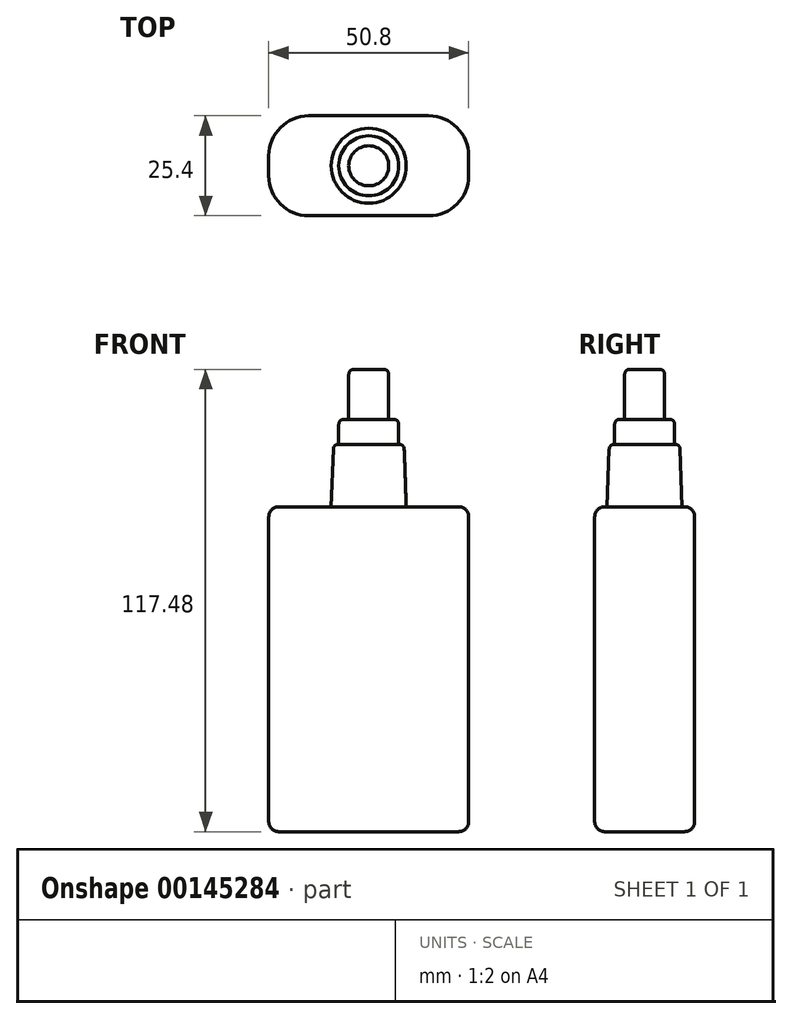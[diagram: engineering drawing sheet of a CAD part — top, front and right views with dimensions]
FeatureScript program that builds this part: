
annotation { "Feature Type Name" : "Feature", "Feature Type Description" : "" }
export const myFeature = defineFeature(function(context is Context, id is Id, definition is map)
    precondition{}
    {
        {
            var Q0;
            Q0=qCreatedBy(makeId("Top.planeOp"),FACE);
            var sketch = newSketch(context, id + "F0", { "sketchPlane" : qUnion([Q0])});
            skLineSegment(sketch, "E0.bottom", {"start": v(-15.24, 12.7) * mm, "end": v(15.24, 12.7) * mm});
            skLineSegment(sketch, "E0.top", {"start": v(-15.24, -12.7) * mm, "end": v(15.24, -12.7) * mm});
            skLineSegment(sketch, "E0.left", {"start": v(-25.4, 2.54) * mm, "end": v(-25.4, -2.54) * mm});
            skLineSegment(sketch, "E0.right", {"start": v(25.4, 2.54) * mm, "end": v(25.4, -2.54) * mm});
            skPoint(sketch, "E0.middle", {"position": v(0, 0) * mm});
            skPoint(sketch, "E1.visualSharp", {"position": v(-25.4, 12.7) * mm});
            skArc(sketch, "E1.filletArc", {"start": v(-15.24, 12.7) * mm, "mid": v(-22.42, 9.72) * mm, "end": v(-25.4, 2.54) * mm});
            skPoint(sketch, "E2.visualSharp", {"position": v(-25.4, -12.7) * mm});
            skArc(sketch, "E2.filletArc", {"start": v(-25.4, -2.54) * mm, "mid": v(-22.42, -9.72) * mm, "end": v(-15.24, -12.7) * mm});
            skPoint(sketch, "E3.visualSharp", {"position": v(25.4, 12.7) * mm});
            skArc(sketch, "E3.filletArc", {"start": v(25.4, 2.54) * mm, "mid": v(22.42, 9.72) * mm, "end": v(15.24, 12.7) * mm});
            skPoint(sketch, "E4.visualSharp", {"position": v(25.4, -12.7) * mm});
            skArc(sketch, "E4.filletArc", {"start": v(15.24, -12.7) * mm, "mid": v(22.42, -9.72) * mm, "end": v(25.4, -2.54) * mm});
            skSolve(sketch);
        }
        {
            var Q0;
            Q0=makeQuery(id+"F0.imprint","IMPRINT",FACE,{"disambiguationData":[TD([[makeQuery(id+"F0.imprint","IMPRINT",EDGE,{"derivedFrom":sQuery(id+"F0.wireOp",EDGE,"E0.bottom")}),-1.0]])]});
            extrude(context, id + "F1", {"entities" : qUnion([Q0]), "depth" : 82.55 * mm});
        }
        {
            var Q0;
            Q0=makeQuery(id+"F1.opExtrude","CAP_FACE",FACE,{"disambiguationData":[OSD([sQuery(id+"F0.wireOp",EDGE,"E0.bottom"),sQuery(id+"F0.wireOp",EDGE,"E0.top"),sQuery(id+"F0.wireOp",EDGE,"E0.left"),sQuery(id+"F0.wireOp",EDGE,"E0.right"),sQuery(id+"F0.wireOp",EDGE,"E1.filletArc"),sQuery(id+"F0.wireOp",EDGE,"E2.filletArc"),sQuery(id+"F0.wireOp",EDGE,"E3.filletArc"),sQuery(id+"F0.wireOp",EDGE,"E4.filletArc")])],"isStart":false});
            var sketch = newSketch(context, id + "F2", { "sketchPlane" : qUnion([Q0])});
            skCircle(sketch, "E5", {"center": v(0, 0) * mm, "radius": 9.53 * mm});
            skSolve(sketch);
        }
        {
            var Q0;
            Q0=makeQuery(id+"F2.imprint","IMPRINT",FACE,{"disambiguationData":[TD([[makeQuery(id+"F2.imprint","IMPRINT",EDGE,{"derivedFrom":sQuery(id+"F2.wireOp",EDGE,"E5")}),1.0]])]});
            extrude(context, id + "F3", {"entities" : qUnion([Q0]), "depth" : 15.88 * mm, "hasDraft" : true, "draftAngle" : 2 * degree, "draftPullDirection" : true});
        }
        {
            var Q0;
            Q0=qCreatedBy(makeId("Front.planeOp"),FACE);
            var sketch = newSketch(context, id + "F4", { "sketchPlane" : qUnion([Q0])});
            skLineSegment(sketch, "E6", {"start": v(0, 140.08) * mm, "end": v(0, 0) * mm, "construction": true});
            skLineSegment(sketch, "E7", {"start": v(0, 117.48) * mm, "end": v(-5.08, 117.48) * mm});
            skLineSegment(sketch, "E8", {"start": v(-5.08, 117.48) * mm, "end": v(-5.08, 104.78) * mm});
            skLineSegment(sketch, "E9", {"start": v(-5.08, 104.78) * mm, "end": v(-7.62, 104.78) * mm});
            skLineSegment(sketch, "E10", {"start": v(-7.62, 104.78) * mm, "end": v(-7.62, 98.43) * mm});
            skLineSegment(sketch, "E11", {"start": v(0, 98.4) * mm, "end": v(0, 117.48) * mm});
            skLineSegment(sketch, "E12", {"start": v(-7.62, 98.43) * mm, "end": v(0, 98.4) * mm});
            skSolve(sketch);
        }
        {
            var Q0;
            Q0 = qSketchRegion(id + "F4", true);
            var Q1;
            Q1=sQuery(id+"F4.wireOp",EDGE,"E11");
            revolve(context, id + "F5", {"operationType" : NewBodyOperationType.ADD, "entities" : qUnion([Q0]), "axis" : qUnion([Q1]), "revolveType" : RevolveType.FULL});
        }
        {
            var Q0;
            Q0=makeQuery(id+"F1.opExtrude","CAP_FACE",FACE,{"disambiguationData":[OSD([sQuery(id+"F0.wireOp",EDGE,"E0.bottom"),sQuery(id+"F0.wireOp",EDGE,"E0.top"),sQuery(id+"F0.wireOp",EDGE,"E0.left"),sQuery(id+"F0.wireOp",EDGE,"E0.right"),sQuery(id+"F0.wireOp",EDGE,"E1.filletArc"),sQuery(id+"F0.wireOp",EDGE,"E2.filletArc"),sQuery(id+"F0.wireOp",EDGE,"E3.filletArc"),sQuery(id+"F0.wireOp",EDGE,"E4.filletArc")])],"isStart":false});
            var Q1;
            Q1=makeQuery(id+"F1.opExtrude","CAP_FACE",FACE,{"disambiguationData":[OSD([sQuery(id+"F0.wireOp",EDGE,"E0.bottom"),sQuery(id+"F0.wireOp",EDGE,"E0.top"),sQuery(id+"F0.wireOp",EDGE,"E0.left"),sQuery(id+"F0.wireOp",EDGE,"E0.right"),sQuery(id+"F0.wireOp",EDGE,"E1.filletArc"),sQuery(id+"F0.wireOp",EDGE,"E2.filletArc"),sQuery(id+"F0.wireOp",EDGE,"E3.filletArc"),sQuery(id+"F0.wireOp",EDGE,"E4.filletArc")])],"isStart":true});
            fillet(context, id + "F6", {"entities" : qUnion([Q0, Q1]), "radius" : 2.54 * mm, "tangentPropagation" : true, "allowEdgeOverflow" : false});
        }
        {
            var Q0;
            Q0=makeQuery(id+"F5.opRevolve","SWEPT_FACE",FACE,{"disambiguationData":[OSD([sQuery(id+"F4.wireOp",EDGE,"E7")])]});
            var Q1;
            Q1=makeQuery(id+"F5.opRevolve","SWEPT_EDGE",EDGE,{"disambiguationData":[OSD([sQuery(id+"F4.wireOp",EDGE,"E9"),sQuery(id+"F4.wireOp",EDGE,"E10")])]});
            var Q2;
            Q2=makeQuery(id+"F3.opExtrude","CAP_EDGE",EDGE,{"disambiguationData":[OSD([sQuery(id+"F2.wireOp",EDGE,"E5")])],"isStart":false});
            fillet(context, id + "F7", {"entities" : qUnion([Q0, Q1, Q2]), "radius" : 1.27 * mm, "tangentPropagation" : true, "allowEdgeOverflow" : false});
        }
    });
